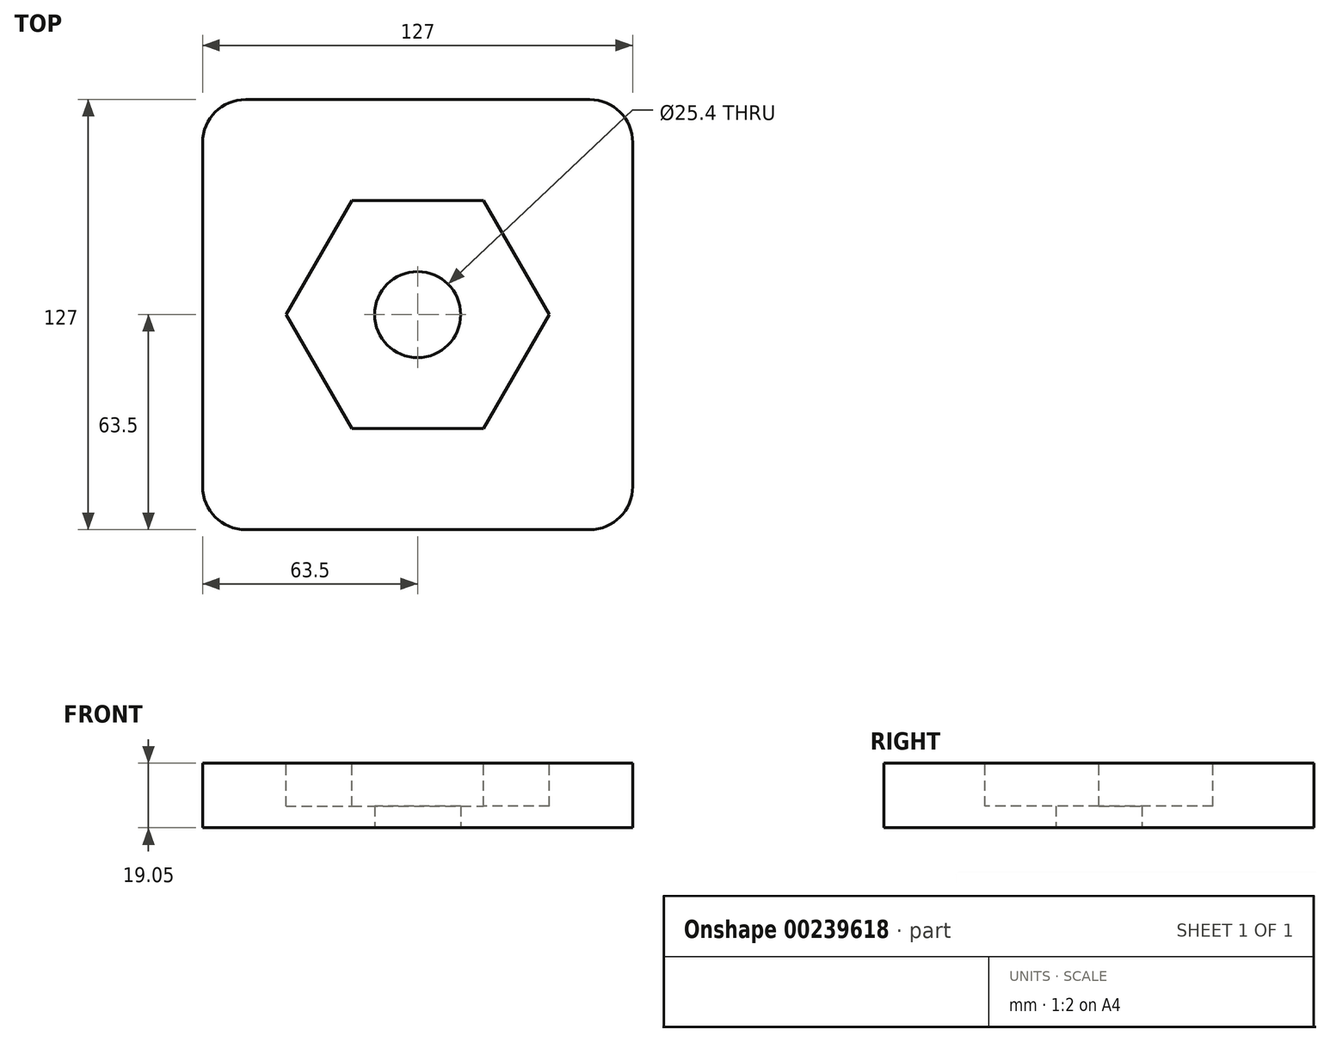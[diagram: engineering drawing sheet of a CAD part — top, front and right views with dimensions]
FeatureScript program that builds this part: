
annotation { "Feature Type Name" : "Feature", "Feature Type Description" : "" }
export const myFeature = defineFeature(function(context is Context, id is Id, definition is map)
    precondition{}
    {
        {
            var Q0;
            Q0=qCreatedBy(makeId("Top.planeOp"),FACE);
            var sketch = newSketch(context, id + "F0", { "sketchPlane" : qUnion([Q0])});
            skLineSegment(sketch, "E0.bottom", {"start": v(63.5, 63.5) * mm, "end": v(-63.5, 63.5) * mm});
            skLineSegment(sketch, "E0.top", {"start": v(63.5, -63.5) * mm, "end": v(-63.5, -63.5) * mm});
            skLineSegment(sketch, "E0.left", {"start": v(63.5, 63.5) * mm, "end": v(63.5, -63.5) * mm});
            skLineSegment(sketch, "E0.right", {"start": v(-63.5, 63.5) * mm, "end": v(-63.5, -63.5) * mm});
            skPoint(sketch, "E0.middle", {"position": v(0, 0) * mm});
            skSolve(sketch);
        }
        {
            var Q0;
            Q0=makeQuery(id+"F0.imprint","IMPRINT",FACE,{"disambiguationData":[TD([[makeQuery(id+"F0.imprint","IMPRINT",EDGE,{"derivedFrom":sQuery(id+"F0.wireOp",EDGE,"E0.bottom")}),1.0]])]});
            extrude(context, id + "F1", {"entities" : qUnion([Q0]), "depth" : 19.05 * mm});
        }
        {
            var Q0;
            Q0=makeQuery(id+"F1.opExtrude","CAP_FACE",FACE,{"disambiguationData":[OSD([sQuery(id+"F0.wireOp",EDGE,"E0.bottom"),sQuery(id+"F0.wireOp",EDGE,"E0.top"),sQuery(id+"F0.wireOp",EDGE,"E0.left"),sQuery(id+"F0.wireOp",EDGE,"E0.right")])],"isStart":false});
            var sketch = newSketch(context, id + "F2", { "sketchPlane" : qUnion([Q0])});
            skCircle(sketch, "E1.cCircle", {"center": v(0, 0) * mm, "radius": 33.66 * mm, "construction": true});
            skLineSegment(sketch, "E1.0", {"start": v(38.86, 0) * mm, "end": v(19.43, -33.66) * mm});
            skLineSegment(sketch, "E1.1", {"start": v(19.43, -33.66) * mm, "end": v(-19.43, -33.66) * mm});
            skLineSegment(sketch, "E1.2", {"start": v(-19.43, -33.66) * mm, "end": v(-38.86, 0) * mm});
            skLineSegment(sketch, "E1.3", {"start": v(-38.86, 0) * mm, "end": v(-19.43, 33.66) * mm});
            skLineSegment(sketch, "E1.4", {"start": v(-19.43, 33.66) * mm, "end": v(19.43, 33.66) * mm});
            skLineSegment(sketch, "E1.5", {"start": v(19.43, 33.66) * mm, "end": v(38.86, 0) * mm});
            skPoint(sketch, "E1.0.midPoint", {"position": v(29.15, -16.83) * mm});
            skSolve(sketch);
        }
        {
            var Q0;
            Q0=makeQuery(id+"F2.imprint","IMPRINT",FACE,{"disambiguationData":[TD([[makeQuery(id+"F2.imprint","IMPRINT",EDGE,{"derivedFrom":sQuery(id+"F2.wireOp",EDGE,"E1.0")}),-1.0]])]});
            extrude(context, id + "F3", {"entities" : qUnion([Q0]), "operationType" : NewBodyOperationType.REMOVE, "oppositeDirection" : true, "depth" : 12.7 * mm});
        }
        {
            var Q0;
            Q0=makeQuery(id+"F1.opExtrude","SWEPT_EDGE",EDGE,{"disambiguationData":[OSD([sQuery(id+"F0.wireOp",EDGE,"E0.top"),sQuery(id+"F0.wireOp",EDGE,"E0.right")])]});
            var Q1;
            Q1=makeQuery(id+"F1.opExtrude","SWEPT_EDGE",EDGE,{"disambiguationData":[OSD([sQuery(id+"F0.wireOp",EDGE,"E0.top"),sQuery(id+"F0.wireOp",EDGE,"E0.left")])]});
            var Q2;
            Q2=makeQuery(id+"F1.opExtrude","SWEPT_EDGE",EDGE,{"disambiguationData":[OSD([sQuery(id+"F0.wireOp",EDGE,"E0.bottom"),sQuery(id+"F0.wireOp",EDGE,"E0.left")])]});
            var Q3;
            Q3=makeQuery(id+"F1.opExtrude","SWEPT_EDGE",EDGE,{"disambiguationData":[OSD([sQuery(id+"F0.wireOp",EDGE,"E0.bottom"),sQuery(id+"F0.wireOp",EDGE,"E0.right")])]});
            fillet(context, id + "F4", {"entities" : qUnion([Q0, Q1, Q2, Q3]), "radius" : 12.7 * mm, "tangentPropagation" : true, "allowEdgeOverflow" : false});
        }
        {
            var Q0;
            Q0=makeQuery(id+"F1.opExtrude","CAP_FACE",FACE,{"disambiguationData":[OSD([sQuery(id+"F0.wireOp",EDGE,"E0.bottom"),sQuery(id+"F0.wireOp",EDGE,"E0.top"),sQuery(id+"F0.wireOp",EDGE,"E0.left"),sQuery(id+"F0.wireOp",EDGE,"E0.right")])],"isStart":true});
            var sketch = newSketch(context, id + "F5", { "sketchPlane" : qUnion([Q0])});
            skCircle(sketch, "E2", {"center": v(0, 0) * mm, "radius": 12.7 * mm});
            skSolve(sketch);
        }
        {
            var Q0;
            Q0=makeQuery(id+"F5.imprint","IMPRINT",FACE,{"disambiguationData":[TD([[makeQuery(id+"F5.imprint","IMPRINT",EDGE,{"derivedFrom":sQuery(id+"F5.wireOp",EDGE,"E2")}),1.0]])]});
            extrude(context, id + "F6", {"entities" : qUnion([Q0]), "operationType" : NewBodyOperationType.REMOVE, "oppositeDirection" : true, "depth" : 25.4 * mm});
        }
    });
